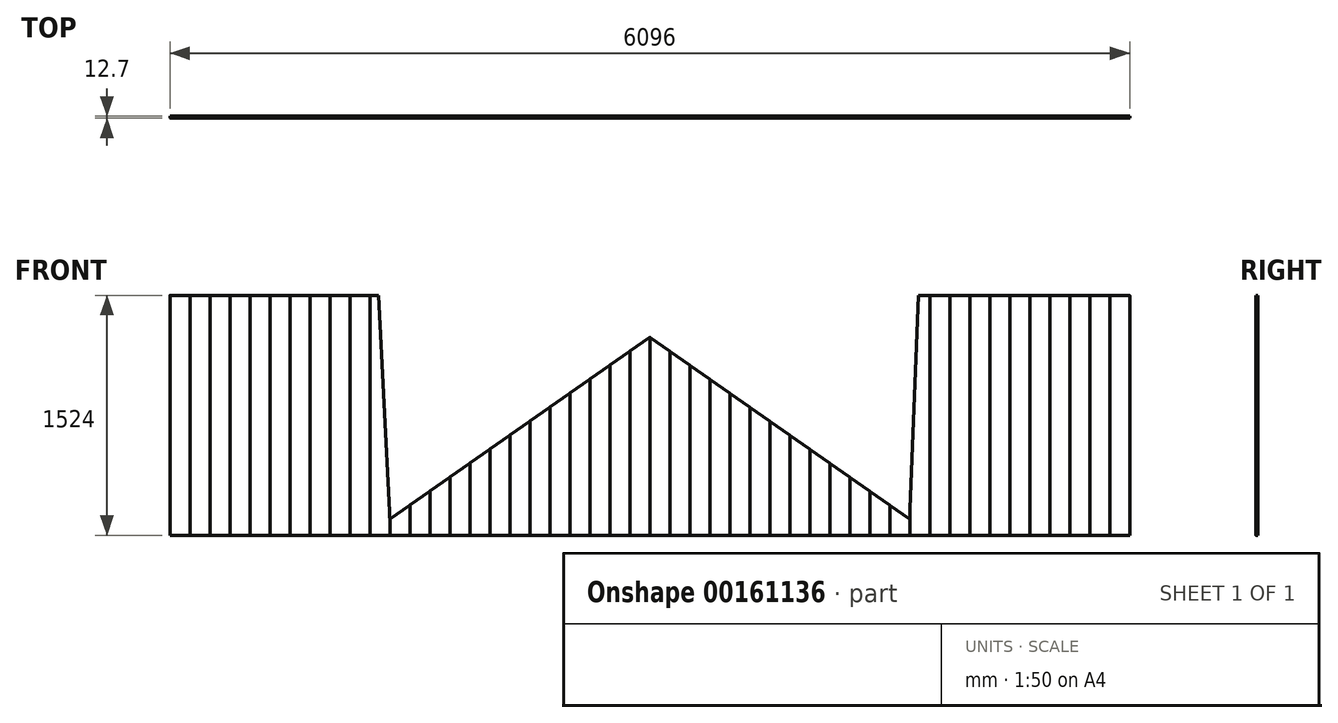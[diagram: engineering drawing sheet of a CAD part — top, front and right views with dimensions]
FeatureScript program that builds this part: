
annotation { "Feature Type Name" : "Feature", "Feature Type Description" : "" }
export const myFeature = defineFeature(function(context is Context, id is Id, definition is map)
    precondition{}
    {
        {
            var Q0;
            Q0=qCreatedBy(makeId("Front.planeOp"),FACE);
            var sketch = newSketch(context, id + "F0", { "sketchPlane" : qUnion([Q0])});
            skLineSegment(sketch, "E0.bottom", {"start": v(0, 0) * mm, "end": v(127, 0) * mm});
            skLineSegment(sketch, "E0.top", {"start": v(0, 1524) * mm, "end": v(127, 1524) * mm});
            skLineSegment(sketch, "E0.left", {"start": v(0, 0) * mm, "end": v(0, 1524) * mm});
            skLineSegment(sketch, "E0.right", {"start": v(127, 0) * mm, "end": v(127, 1524) * mm});
            skSolve(sketch);
        }
        {
            var Q0;
            Q0=qSketchRegion(id+"F0",true);
            extrude(context, id + "F1", {"entities" : qUnion([Q0]), "depth" : 12.7 * mm});
        }
        {
            var Q0;
            Q0=makeQuery(id+"F1.opExtrude","CAP_EDGE",EDGE,{"disambiguationData":[OSD([sQuery(id+"F0.wireOp",EDGE,"E0.left")])],"isStart":false});
            var Q1;
            Q1=makeQuery(id+"F1.opExtrude","CAP_EDGE",EDGE,{"disambiguationData":[OSD([sQuery(id+"F0.wireOp",EDGE,"E0.right")])],"isStart":false});
            fillet(context, id + "F2", {"entities" : qUnion([Q0, Q1]), "radius" : 2.54 * mm, "tangentPropagation" : true, "allowEdgeOverflow" : false});
        }
        {
            var Q0;
            Q0=makeQuery(id+"F1.opExtrude","SWEPT_BODY",BODY,{"disambiguationData":[OSD([sQuery(id+"F0.wireOp",EDGE,"E0.bottom"),sQuery(id+"F0.wireOp",EDGE,"E0.top"),sQuery(id+"F0.wireOp",EDGE,"E0.left"),sQuery(id+"F0.wireOp",EDGE,"E0.right")])]});
            var Q1;
            Q1=makeQuery(id+"F1.opExtrude","SWEPT_FACE",FACE,{"disambiguationData":[OSD([sQuery(id+"F0.wireOp",EDGE,"E0.right")])]});
            mirror(context, id + "F3", {"entities" : qUnion([Q0]), "mirrorPlane" : qUnion([Q1])});
        }
        {
            var Q0;
            Q0=makeQuery(id+"F1.opExtrude","SWEPT_BODY",BODY,{"disambiguationData":[OSD([sQuery(id+"F0.wireOp",EDGE,"E0.bottom"),sQuery(id+"F0.wireOp",EDGE,"E0.top"),sQuery(id+"F0.wireOp",EDGE,"E0.left"),sQuery(id+"F0.wireOp",EDGE,"E0.right")])]});
            var Q1;
            Q1=makeQuery(id+"F3.opPattern","COPY",BODY,{"derivedFrom":makeQuery(id+"F1.opExtrude","SWEPT_BODY",BODY,{"disambiguationData":[OSD([sQuery(id+"F0.wireOp",EDGE,"E0.bottom"),sQuery(id+"F0.wireOp",EDGE,"E0.top"),sQuery(id+"F0.wireOp",EDGE,"E0.left"),sQuery(id+"F0.wireOp",EDGE,"E0.right")])]}),"instanceName":"1"});
            var Q2;
            Q2=makeQuery(id+"F3.opPattern","COPY",FACE,{"derivedFrom":makeQuery(id+"F1.opExtrude","SWEPT_FACE",FACE,{"disambiguationData":[OSD([sQuery(id+"F0.wireOp",EDGE,"E0.left")])]}),"instanceName":"1"});
            mirror(context, id + "F4", {"operationType" : NewBodyOperationType.ADD, "entities" : qUnion([Q0, Q1]), "mirrorPlane" : qUnion([Q2])});
        }
        {
            var Q0;
            Q0=makeQuery(id+"F1.opExtrude","SWEPT_BODY",BODY,{"disambiguationData":[OSD([sQuery(id+"F0.wireOp",EDGE,"E0.bottom"),sQuery(id+"F0.wireOp",EDGE,"E0.top"),sQuery(id+"F0.wireOp",EDGE,"E0.left"),sQuery(id+"F0.wireOp",EDGE,"E0.right")])]});
            var Q1;
            Q1=makeQuery(id+"F3.opPattern","COPY",BODY,{"derivedFrom":makeQuery(id+"F1.opExtrude","SWEPT_BODY",BODY,{"disambiguationData":[OSD([sQuery(id+"F0.wireOp",EDGE,"E0.bottom"),sQuery(id+"F0.wireOp",EDGE,"E0.top"),sQuery(id+"F0.wireOp",EDGE,"E0.left"),sQuery(id+"F0.wireOp",EDGE,"E0.right")])]}),"instanceName":"1"});
            var Q2;
            Q2=makeQuery(id+"F4.opPattern","COPY",FACE,{"derivedFrom":makeQuery(id+"F1.opExtrude","SWEPT_FACE",FACE,{"disambiguationData":[OSD([sQuery(id+"F0.wireOp",EDGE,"E0.left")])]}),"instanceName":"1"});
            mirror(context, id + "F5", {"entities" : qUnion([Q0, Q1]), "mirrorPlane" : qUnion([Q2])});
        }
        {
            var Q0;
            Q0=makeQuery(id+"F5.opPattern","COPY",BODY,{"derivedFrom":makeQuery(id+"F3.opPattern","COPY",BODY,{"derivedFrom":makeQuery(id+"F1.opExtrude","SWEPT_BODY",BODY,{"disambiguationData":[OSD([sQuery(id+"F0.wireOp",EDGE,"E0.bottom"),sQuery(id+"F0.wireOp",EDGE,"E0.top"),sQuery(id+"F0.wireOp",EDGE,"E0.left"),sQuery(id+"F0.wireOp",EDGE,"E0.right")])]}),"instanceName":"1"}),"instanceName":"1"});
            var Q1;
            Q1=makeQuery(id+"F5.opPattern","COPY",BODY,{"derivedFrom":makeQuery(id+"F1.opExtrude","SWEPT_BODY",BODY,{"disambiguationData":[OSD([sQuery(id+"F0.wireOp",EDGE,"E0.bottom"),sQuery(id+"F0.wireOp",EDGE,"E0.top"),sQuery(id+"F0.wireOp",EDGE,"E0.left"),sQuery(id+"F0.wireOp",EDGE,"E0.right")])]}),"instanceName":"1"});
            var Q2;
            Q2=makeQuery(id+"F5.opPattern","COPY",FACE,{"derivedFrom":makeQuery(id+"F1.opExtrude","SWEPT_FACE",FACE,{"disambiguationData":[OSD([sQuery(id+"F0.wireOp",EDGE,"E0.left")])]}),"instanceName":"1"});
            mirror(context, id + "F6", {"operationType" : NewBodyOperationType.ADD, "entities" : qUnion([Q0, Q1]), "mirrorPlane" : qUnion([Q2])});
        }
        {
            var Q0;
            Q0=makeQuery(id+"F1.opExtrude","SWEPT_BODY",BODY,{"disambiguationData":[OSD([sQuery(id+"F0.wireOp",EDGE,"E0.bottom"),sQuery(id+"F0.wireOp",EDGE,"E0.top"),sQuery(id+"F0.wireOp",EDGE,"E0.left"),sQuery(id+"F0.wireOp",EDGE,"E0.right")])]});
            var Q1;
            Q1=makeQuery(id+"F1.opExtrude","SWEPT_FACE",FACE,{"disambiguationData":[OSD([sQuery(id+"F0.wireOp",EDGE,"E0.left")])]});
            mirror(context, id + "F7", {"operationType" : NewBodyOperationType.ADD, "entities" : qUnion([Q0]), "mirrorPlane" : qUnion([Q1])});
        }
        {
            var Q0;
            Q0=makeQuery(id+"F1.opExtrude","SWEPT_BODY",BODY,{"disambiguationData":[OSD([sQuery(id+"F0.wireOp",EDGE,"E0.bottom"),sQuery(id+"F0.wireOp",EDGE,"E0.top"),sQuery(id+"F0.wireOp",EDGE,"E0.left"),sQuery(id+"F0.wireOp",EDGE,"E0.right")])]});
            var Q1;
            Q1=makeQuery(id+"F3.opPattern","COPY",BODY,{"derivedFrom":makeQuery(id+"F1.opExtrude","SWEPT_BODY",BODY,{"disambiguationData":[OSD([sQuery(id+"F0.wireOp",EDGE,"E0.bottom"),sQuery(id+"F0.wireOp",EDGE,"E0.top"),sQuery(id+"F0.wireOp",EDGE,"E0.left"),sQuery(id+"F0.wireOp",EDGE,"E0.right")])]}),"instanceName":"1"});
            var Q2;
            Q2=makeQuery(id+"F5.opPattern","COPY",BODY,{"derivedFrom":makeQuery(id+"F3.opPattern","COPY",BODY,{"derivedFrom":makeQuery(id+"F1.opExtrude","SWEPT_BODY",BODY,{"disambiguationData":[OSD([sQuery(id+"F0.wireOp",EDGE,"E0.bottom"),sQuery(id+"F0.wireOp",EDGE,"E0.top"),sQuery(id+"F0.wireOp",EDGE,"E0.left"),sQuery(id+"F0.wireOp",EDGE,"E0.right")])]}),"instanceName":"1"}),"instanceName":"1"});
            var Q3;
            Q3=makeQuery(id+"F5.opPattern","COPY",BODY,{"derivedFrom":makeQuery(id+"F1.opExtrude","SWEPT_BODY",BODY,{"disambiguationData":[OSD([sQuery(id+"F0.wireOp",EDGE,"E0.bottom"),sQuery(id+"F0.wireOp",EDGE,"E0.top"),sQuery(id+"F0.wireOp",EDGE,"E0.left"),sQuery(id+"F0.wireOp",EDGE,"E0.right")])]}),"instanceName":"1"});
            var Q4;
            Q4=makeQuery(id+"F6.opPattern","COPY",FACE,{"derivedFrom":makeQuery(id+"F5.opPattern","COPY",FACE,{"derivedFrom":makeQuery(id+"F4.opPattern","COPY",FACE,{"derivedFrom":makeQuery(id+"F1.opExtrude","SWEPT_FACE",FACE,{"disambiguationData":[OSD([sQuery(id+"F0.wireOp",EDGE,"E0.left")])]}),"instanceName":"1"}),"instanceName":"1"}),"instanceName":"1"});
            mirror(context, id + "F8", {"operationType" : NewBodyOperationType.ADD, "entities" : qUnion([Q0, Q1, Q2, Q3]), "mirrorPlane" : qUnion([Q4])});
        }
        {
            var Q0;
            Q0=makeQuery(id+"F7.opPattern","COPY",FACE,{"derivedFrom":makeQuery(id+"F1.opExtrude","CAP_FACE",FACE,{"disambiguationData":[OSD([sQuery(id+"F0.wireOp",EDGE,"E0.bottom"),sQuery(id+"F0.wireOp",EDGE,"E0.top"),sQuery(id+"F0.wireOp",EDGE,"E0.left"),sQuery(id+"F0.wireOp",EDGE,"E0.right")])],"isStart":false}),"instanceName":"1"});
            var sketch = newSketch(context, id + "F9", { "sketchPlane" : qUnion([Q0])});
            skLineSegment(sketch, "E1", {"start": v(-127, 101.6) * mm, "end": v(1524, 1257.64) * mm});
            skLineSegment(sketch, "E2", {"start": v(1524, 1598.62) * mm, "end": v(1524, -27.38) * mm});
            skLineSegment(sketch, "E3", {"start": v(1524, 1257.64) * mm, "end": v(3175, 101.6) * mm});
            skLineSegment(sketch, "E4", {"start": v(-127, 101.6) * mm, "end": v(-202.06, 1586.92) * mm});
            skLineSegment(sketch, "E5", {"start": v(-202.06, 1586.92) * mm, "end": v(3229.89, 1552.77) * mm});
            skLineSegment(sketch, "E6", {"start": v(3229.89, 1552.77) * mm, "end": v(3175, 101.6) * mm});
            skPoint(sketch, "E7.orphan", {"position": v(-127, 101.6) * mm});
            skSolve(sketch);
        }
        {
            var Q0;
            Q0=qSketchRegion(id+"F9",true);
            extrude(context, id + "F10", {"entities" : qUnion([Q0]), "oppositeDirection" : true, "depth" : 12.7 * mm});
        }
        {
            var Q0;
            Q0=makeQuery(id+"F10.opExtrude","SWEPT_BODY",BODY,{"disambiguationData":[OSD([sQuery(id+"F9.wireOp",EDGE,"E1"),sQuery(id+"F9.wireOp",EDGE,"E3"),sQuery(id+"F9.wireOp",EDGE,"E4"),sQuery(id+"F9.wireOp",EDGE,"E5"),sQuery(id+"F9.wireOp",EDGE,"E6")])]});
            var Q1;
            Q1=makeQuery(id+"F1.opExtrude","SWEPT_BODY",BODY,{"disambiguationData":[OSD([sQuery(id+"F0.wireOp",EDGE,"E0.bottom"),sQuery(id+"F0.wireOp",EDGE,"E0.top"),sQuery(id+"F0.wireOp",EDGE,"E0.left"),sQuery(id+"F0.wireOp",EDGE,"E0.right")])]});
            var Q2;
            Q2=makeQuery(id+"F3.opPattern","COPY",BODY,{"derivedFrom":makeQuery(id+"F1.opExtrude","SWEPT_BODY",BODY,{"disambiguationData":[OSD([sQuery(id+"F0.wireOp",EDGE,"E0.bottom"),sQuery(id+"F0.wireOp",EDGE,"E0.top"),sQuery(id+"F0.wireOp",EDGE,"E0.left"),sQuery(id+"F0.wireOp",EDGE,"E0.right")])]}),"instanceName":"1"});
            var Q3;
            Q3=makeQuery(id+"F5.opPattern","COPY",BODY,{"derivedFrom":makeQuery(id+"F3.opPattern","COPY",BODY,{"derivedFrom":makeQuery(id+"F1.opExtrude","SWEPT_BODY",BODY,{"disambiguationData":[OSD([sQuery(id+"F0.wireOp",EDGE,"E0.bottom"),sQuery(id+"F0.wireOp",EDGE,"E0.top"),sQuery(id+"F0.wireOp",EDGE,"E0.left"),sQuery(id+"F0.wireOp",EDGE,"E0.right")])]}),"instanceName":"1"}),"instanceName":"1"});
            var Q4;
            Q4=makeQuery(id+"F5.opPattern","COPY",BODY,{"derivedFrom":makeQuery(id+"F1.opExtrude","SWEPT_BODY",BODY,{"disambiguationData":[OSD([sQuery(id+"F0.wireOp",EDGE,"E0.bottom"),sQuery(id+"F0.wireOp",EDGE,"E0.top"),sQuery(id+"F0.wireOp",EDGE,"E0.left"),sQuery(id+"F0.wireOp",EDGE,"E0.right")])]}),"instanceName":"1"});
            booleanBodies(context, id + "F11", {"operationType" : BooleanOperationType.SUBTRACTION, "tools" : qUnion([Q0]), "targets" : qUnion([Q1, Q2, Q3, Q4])});
        }
    });
